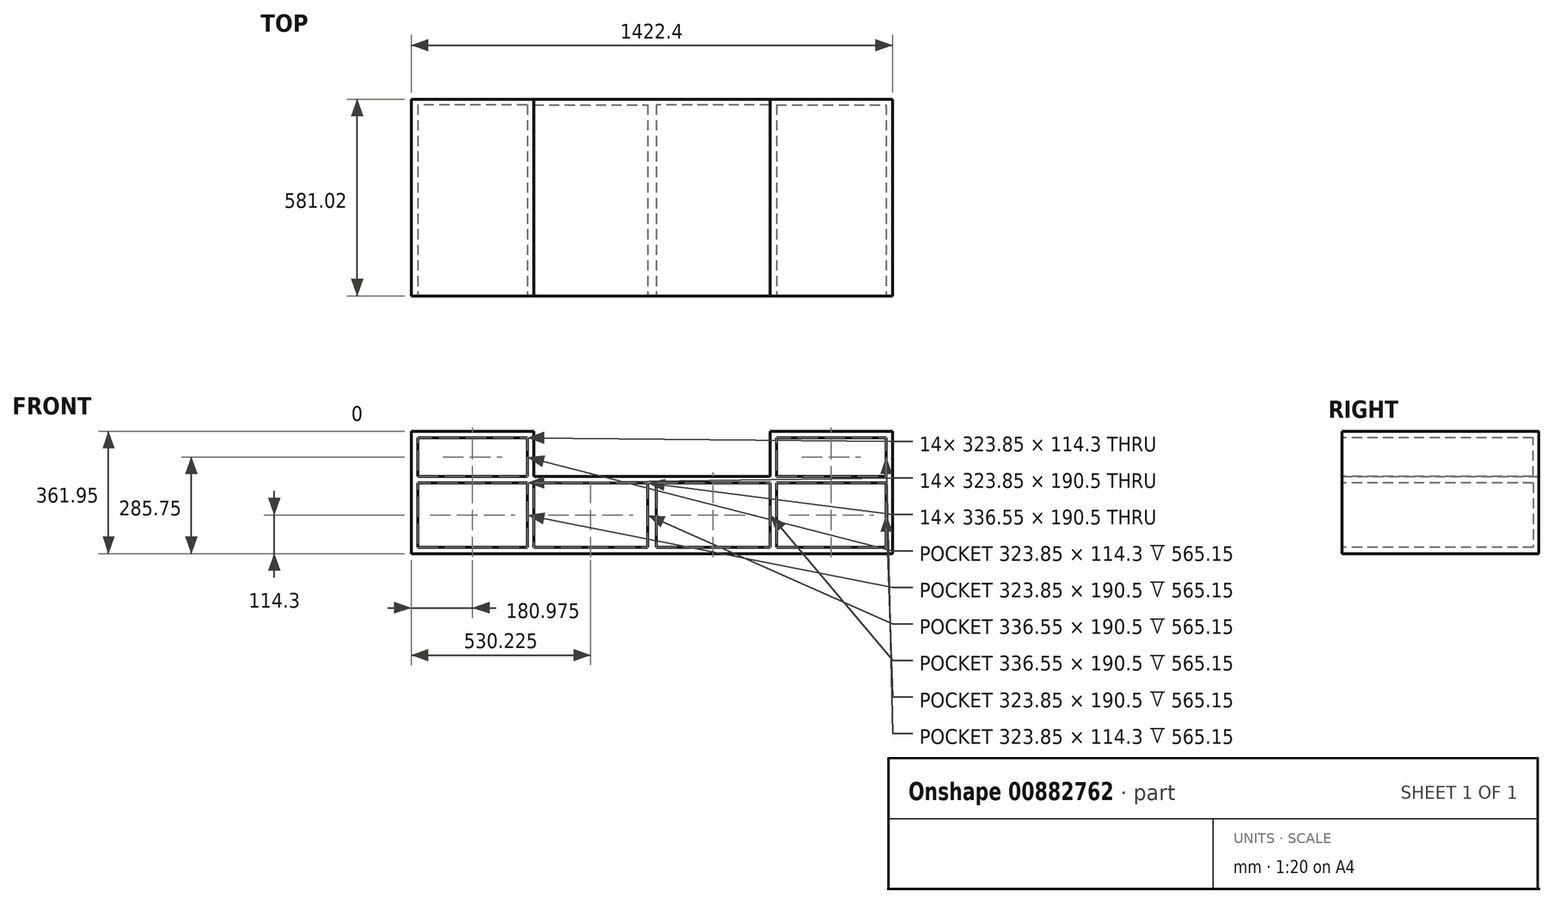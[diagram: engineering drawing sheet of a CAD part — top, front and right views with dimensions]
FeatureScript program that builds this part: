
annotation { "Feature Type Name" : "Feature", "Feature Type Description" : "" }
export const myFeature = defineFeature(function(context is Context, id is Id, definition is map)
    precondition{}
    {
        {
            var Q0;
            Q0=qCreatedBy(makeId("Front.planeOp"),FACE);
            var sketch = newSketch(context, id + "F0", { "sketchPlane" : qUnion([Q0])});
            skLineSegment(sketch, "E0.bottom", {"start": v(0, 0) * mm, "end": v(1422.4, 0) * mm});
            skLineSegment(sketch, "E0.left", {"start": v(0, 0) * mm, "end": v(0, 361.95) * mm});
            skLineSegment(sketch, "E0.right", {"start": v(1422.4, 0) * mm, "end": v(1422.4, 361.95) * mm});
            skLineSegment(sketch, "E1", {"start": v(0, 361.95) * mm, "end": v(361.95, 361.95) * mm});
            skLineSegment(sketch, "E2", {"start": v(361.95, 361.95) * mm, "end": v(361.95, 228.6) * mm});
            skLineSegment(sketch, "E3", {"start": v(361.95, 228.6) * mm, "end": v(1060.45, 228.6) * mm});
            skLineSegment(sketch, "E4", {"start": v(1060.45, 228.6) * mm, "end": v(1060.45, 361.95) * mm});
            skLineSegment(sketch, "E5", {"start": v(1060.45, 361.95) * mm, "end": v(1422.4, 361.95) * mm});
            skSolve(sketch);
        }
        {
            var Q0;
            Q0 = qSketchRegion(id + "F0", true);
            extrude(context, id + "F1", {"entities" : qUnion([Q0]), "depth" : 581.02 * mm, "offsetDistance" : 25.4 * mm});
        }
        {
            var Q0;
            Q0=makeQuery(id+"F1.opExtrude","CAP_FACE",FACE,{"disambiguationData":[OSD([sQuery(id+"F0.wireOp",EDGE,"E0.bottom"),sQuery(id+"F0.wireOp",EDGE,"E0.left"),sQuery(id+"F0.wireOp",EDGE,"E0.right"),sQuery(id+"F0.wireOp",EDGE,"E1"),sQuery(id+"F0.wireOp",EDGE,"E2"),sQuery(id+"F0.wireOp",EDGE,"E3"),sQuery(id+"F0.wireOp",EDGE,"E4"),sQuery(id+"F0.wireOp",EDGE,"E5")])],"isStart":false});
            var sketch = newSketch(context, id + "F2", { "sketchPlane" : qUnion([Q0])});
            skLineSegment(sketch, "E6.bottom", {"start": v(342.9, 228.6) * mm, "end": v(19.05, 228.6) * mm});
            skLineSegment(sketch, "E6.top", {"start": v(342.9, 342.9) * mm, "end": v(19.05, 342.9) * mm});
            skLineSegment(sketch, "E6.left", {"start": v(342.9, 228.6) * mm, "end": v(342.9, 342.9) * mm});
            skLineSegment(sketch, "E6.right", {"start": v(19.05, 228.6) * mm, "end": v(19.05, 342.9) * mm});
            skLineSegment(sketch, "E7.bottom", {"start": v(1079.5, 228.6) * mm, "end": v(1403.35, 228.6) * mm});
            skLineSegment(sketch, "E7.top", {"start": v(1079.5, 342.9) * mm, "end": v(1403.35, 342.9) * mm});
            skLineSegment(sketch, "E7.left", {"start": v(1079.5, 228.6) * mm, "end": v(1079.5, 342.9) * mm});
            skLineSegment(sketch, "E7.right", {"start": v(1403.35, 228.6) * mm, "end": v(1403.35, 342.9) * mm});
            skLineSegment(sketch, "E8.bottom", {"start": v(19.05, 209.55) * mm, "end": v(342.9, 209.55) * mm});
            skLineSegment(sketch, "E8.top", {"start": v(19.05, 19.05) * mm, "end": v(342.9, 19.05) * mm});
            skLineSegment(sketch, "E8.left", {"start": v(19.05, 209.55) * mm, "end": v(19.05, 19.05) * mm});
            skLineSegment(sketch, "E8.right", {"start": v(342.9, 209.55) * mm, "end": v(342.9, 19.05) * mm});
            skLineSegment(sketch, "E9.bottom", {"start": v(361.95, 209.55) * mm, "end": v(698.5, 209.55) * mm});
            skLineSegment(sketch, "E9.top", {"start": v(361.95, 19.05) * mm, "end": v(698.5, 19.05) * mm});
            skLineSegment(sketch, "E9.left", {"start": v(361.95, 209.55) * mm, "end": v(361.95, 19.05) * mm});
            skLineSegment(sketch, "E9.right", {"start": v(698.5, 209.55) * mm, "end": v(698.5, 19.05) * mm});
            skLineSegment(sketch, "E10.bottom", {"start": v(1079.5, 209.55) * mm, "end": v(1403.35, 209.55) * mm});
            skLineSegment(sketch, "E10.top", {"start": v(1079.5, 19.05) * mm, "end": v(1403.35, 19.05) * mm});
            skLineSegment(sketch, "E10.left", {"start": v(1079.5, 209.55) * mm, "end": v(1079.5, 19.05) * mm});
            skLineSegment(sketch, "E10.right", {"start": v(1403.35, 209.55) * mm, "end": v(1403.35, 19.05) * mm});
            skLineSegment(sketch, "E11.bottom", {"start": v(1060.45, 19.05) * mm, "end": v(723.9, 19.05) * mm});
            skLineSegment(sketch, "E11.top", {"start": v(1060.45, 209.55) * mm, "end": v(723.9, 209.55) * mm});
            skLineSegment(sketch, "E11.left", {"start": v(1060.45, 19.05) * mm, "end": v(1060.45, 209.55) * mm});
            skLineSegment(sketch, "E11.right", {"start": v(723.9, 19.05) * mm, "end": v(723.9, 209.55) * mm});
            skSolve(sketch);
        }
        {
            var Q0;
            Q0=makeQuery(id+"F2.imprint","IMPRINT",FACE,{"disambiguationData":[TD([[makeQuery(id+"F2.imprint","IMPRINT",EDGE,{"derivedFrom":sQuery(id+"F2.wireOp",EDGE,"E6.bottom")}),-1.0]])]});
            var Q1;
            Q1=makeQuery(id+"F2.imprint","IMPRINT",FACE,{"disambiguationData":[TD([[makeQuery(id+"F2.imprint","IMPRINT",EDGE,{"derivedFrom":sQuery(id+"F2.wireOp",EDGE,"E8.bottom")}),-1.0]])]});
            var Q2;
            Q2=makeQuery(id+"F2.imprint","IMPRINT",FACE,{"disambiguationData":[TD([[makeQuery(id+"F2.imprint","IMPRINT",EDGE,{"derivedFrom":sQuery(id+"F2.wireOp",EDGE,"E9.bottom")}),-1.0]])]});
            var Q3;
            Q3=makeQuery(id+"F2.imprint","IMPRINT",FACE,{"disambiguationData":[TD([[makeQuery(id+"F2.imprint","IMPRINT",EDGE,{"derivedFrom":sQuery(id+"F2.wireOp",EDGE,"E11.bottom")}),-1.0]])]});
            var Q4;
            Q4=makeQuery(id+"F2.imprint","IMPRINT",FACE,{"disambiguationData":[TD([[makeQuery(id+"F2.imprint","IMPRINT",EDGE,{"derivedFrom":sQuery(id+"F2.wireOp",EDGE,"E10.bottom")}),-1.0]])]});
            var Q5;
            Q5=makeQuery(id+"F2.imprint","IMPRINT",FACE,{"disambiguationData":[TD([[makeQuery(id+"F2.imprint","IMPRINT",EDGE,{"derivedFrom":sQuery(id+"F2.wireOp",EDGE,"E7.bottom")}),1.0]])]});
            extrude(context, id + "F3", {"entities" : qUnion([Q0, Q1, Q2, Q3, Q4, Q5]), "operationType" : NewBodyOperationType.REMOVE, "oppositeDirection" : true, "depth" : 565.15 * mm, "offsetDistance" : 25.4 * mm});
        }
    });
